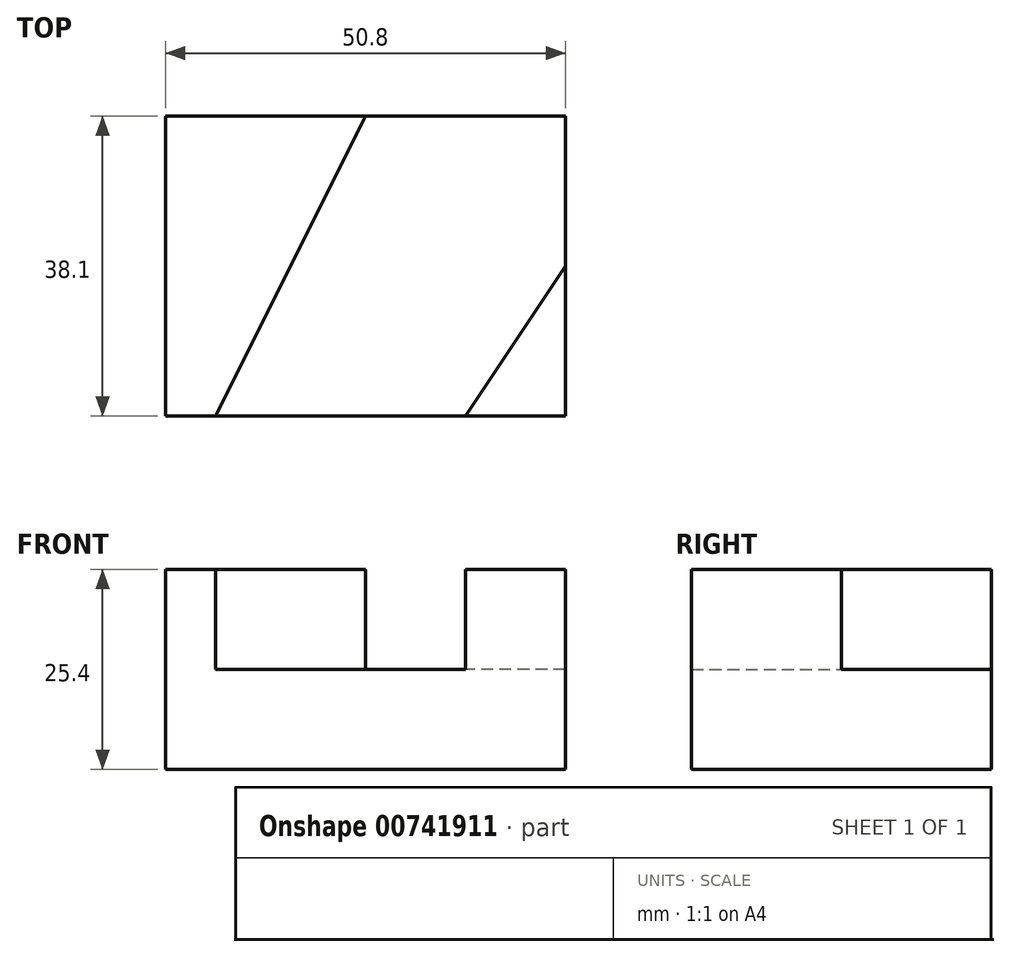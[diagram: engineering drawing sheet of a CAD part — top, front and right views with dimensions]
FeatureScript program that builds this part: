
annotation { "Feature Type Name" : "Feature", "Feature Type Description" : "" }
export const myFeature = defineFeature(function(context is Context, id is Id, definition is map)
    precondition{}
    {
        {
            var Q0;
            Q0=qCreatedBy(makeId("Front.planeOp"),FACE);
            var sketch = newSketch(context, id + "F0", { "sketchPlane" : qUnion([Q0])});
            skLineSegment(sketch, "E0", {"start": v(0, 0) * mm, "end": v(0, 25.4) * mm});
            skLineSegment(sketch, "E1", {"start": v(0, 25.4) * mm, "end": v(50.8, 25.4) * mm});
            skLineSegment(sketch, "E2", {"start": v(50.8, 25.4) * mm, "end": v(50.8, 0) * mm});
            skLineSegment(sketch, "E3", {"start": v(50.8, 0) * mm, "end": v(0, 0) * mm});
            skSolve(sketch);
        }
        {
            var Q0;
            Q0=makeQuery(id+"F0.imprint","IMPRINT",FACE,{"disambiguationData":[TD([[makeQuery(id+"F0.imprint","IMPRINT",EDGE,{"derivedFrom":sQuery(id+"F0.wireOp",EDGE,"E0")}),-1.0]])]});
            extrude(context, id + "F1", {"entities" : qUnion([Q0]), "depth" : 38.1 * mm, "offsetDistance" : 25.4 * mm});
        }
        {
            var Q0;
            Q0=makeQuery(id+"F1.opExtrude","SWEPT_FACE",FACE,{"disambiguationData":[OSD([sQuery(id+"F0.wireOp",EDGE,"E1")])]});
            var sketch = newSketch(context, id + "F2", { "sketchPlane" : qUnion([Q0])});
            skLineSegment(sketch, "E4", {"start": v(0, -38.1) * mm, "end": v(6.35, -38.1) * mm});
            skLineSegment(sketch, "E5", {"start": v(6.35, -38.1) * mm, "end": v(25.4, 0) * mm});
            skLineSegment(sketch, "E6", {"start": v(25.4, 0) * mm, "end": v(50.8, 0) * mm});
            skLineSegment(sketch, "E7", {"start": v(50.8, 0) * mm, "end": v(50.8, -19.05) * mm});
            skLineSegment(sketch, "E8", {"start": v(50.8, -19.05) * mm, "end": v(38.1, -38.1) * mm});
            skLineSegment(sketch, "E9", {"start": v(38.1, -38.1) * mm, "end": v(6.35, -38.1) * mm});
            skSolve(sketch);
        }
        {
            var Q0;
            Q0=makeQuery(id+"F2.imprint","IMPRINT",FACE,{"disambiguationData":[TD([[makeQuery(id+"F2.imprint","IMPRINT",EDGE,{"derivedFrom":sQuery(id+"F2.wireOp",EDGE,"E5")}),-1.0]])]});
            extrude(context, id + "F3", {"entities" : qUnion([Q0]), "operationType" : NewBodyOperationType.REMOVE, "oppositeDirection" : true, "depth" : 12.7 * mm, "offsetDistance" : 25.4 * mm});
        }
    });
